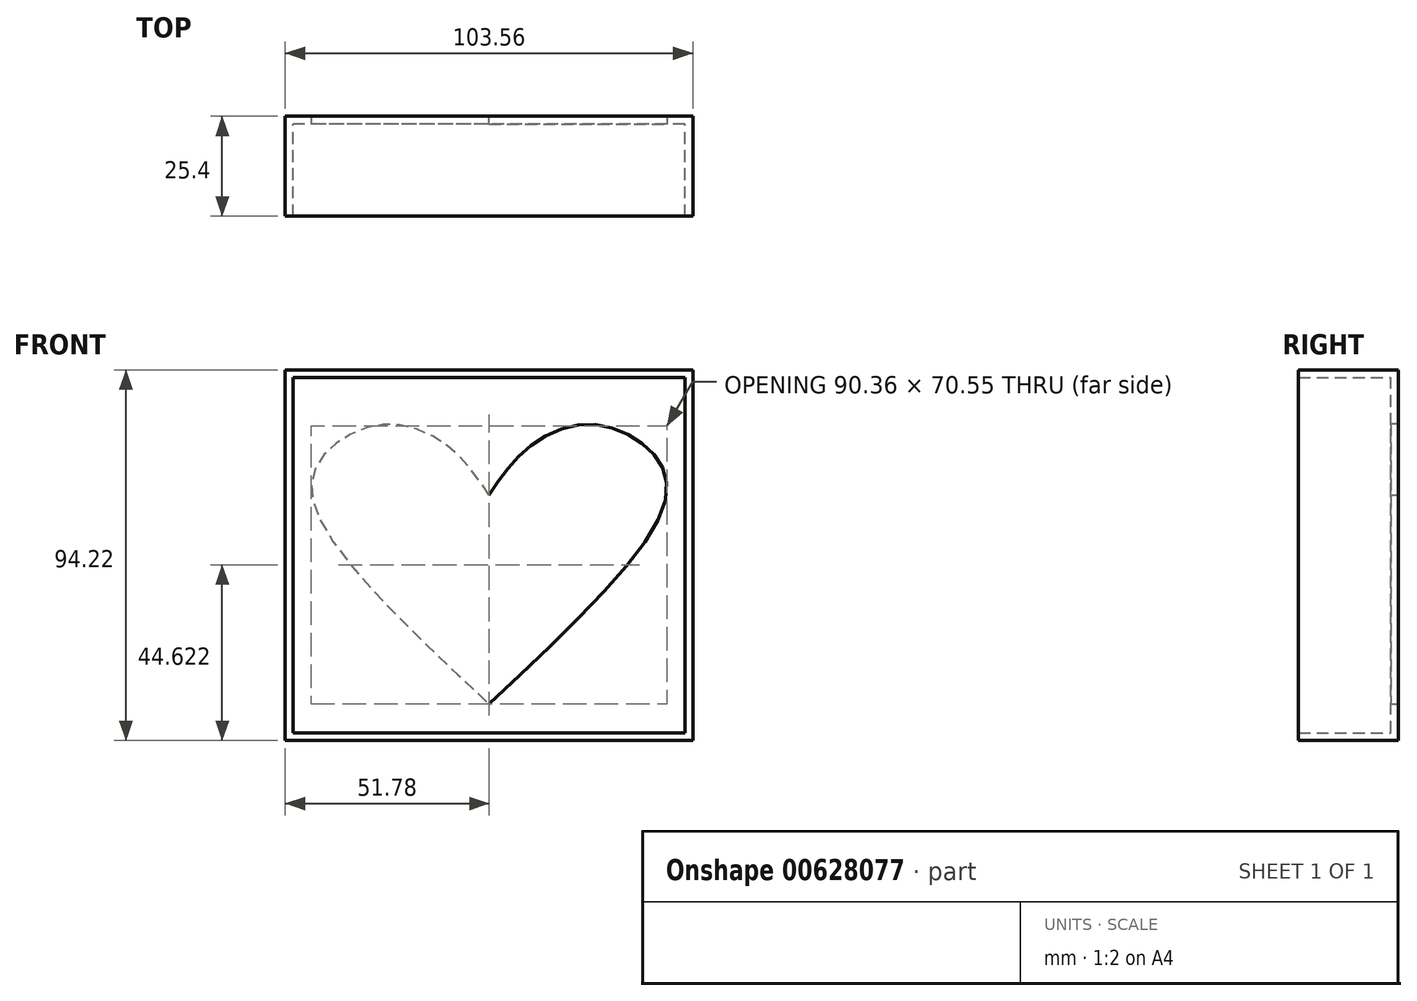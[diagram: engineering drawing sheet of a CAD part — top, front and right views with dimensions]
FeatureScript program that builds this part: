
annotation { "Feature Type Name" : "Feature", "Feature Type Description" : "" }
export const myFeature = defineFeature(function(context is Context, id is Id, definition is map)
    precondition{}
    {
        {
            var Q0;
            Q0=qCreatedBy(makeId("Front.planeOp"),FACE);
            var sketch = newSketch(context, id + "F0", { "sketchPlane" : qUnion([Q0])});
            skLineSegment(sketch, "E0.bottom", {"start": v(51.78, -47.1) * mm, "end": v(-51.78, -47.1) * mm});
            skLineSegment(sketch, "E0.top", {"start": v(51.78, 47.1) * mm, "end": v(-51.78, 47.1) * mm});
            skLineSegment(sketch, "E0.left", {"start": v(51.78, -47.1) * mm, "end": v(51.78, 47.1) * mm});
            skLineSegment(sketch, "E0.right", {"start": v(-51.78, -47.1) * mm, "end": v(-51.78, 47.1) * mm});
            skPoint(sketch, "E0.middle", {"position": v(0, 0) * mm});
            skSolve(sketch);
        }
        {
            var Q0;
            Q0=makeQuery(id+"F0.imprint","IMPRINT",FACE,{"disambiguationData":[TD([[makeQuery(id+"F0.imprint","IMPRINT",EDGE,{"derivedFrom":sQuery(id+"F0.wireOp",EDGE,"E0.bottom")}),-1.0]])]});
            extrude(context, id + "F1", {"entities" : qUnion([Q0]), "depth" : 25.4 * mm, "offsetDistance" : 25.4 * mm});
        }
        {
            var Q0;
            Q0=makeQuery(id+"F1.opExtrude","CAP_FACE",FACE,{"disambiguationData":[OSD([sQuery(id+"F0.wireOp",EDGE,"E0.bottom"),sQuery(id+"F0.wireOp",EDGE,"E0.top"),sQuery(id+"F0.wireOp",EDGE,"E0.left"),sQuery(id+"F0.wireOp",EDGE,"E0.right")])],"isStart":false});
            shell(context, id + "F2", {"entities" : qUnion([Q0]), "thickness" : 2 * mm});
        }
        {
            var Q0;
            Q0=makeQuery(id+"F1.opExtrude","CAP_FACE",FACE,{"disambiguationData":[OSD([sQuery(id+"F0.wireOp",EDGE,"E0.bottom"),sQuery(id+"F0.wireOp",EDGE,"E0.top"),sQuery(id+"F0.wireOp",EDGE,"E0.left"),sQuery(id+"F0.wireOp",EDGE,"E0.right")])],"isStart":true});
            var sketch = newSketch(context, id + "F3", { "sketchPlane" : qUnion([Q0])});
            skFitSpline(sketch, "E1", {"points": [v(0, 15.33) * mm, v(9.9, 27.3) * mm, v(25.61, 33.27) * mm, v(40.57, 26.92) * mm, v(44.68, 13.46) * mm, v(0, -37.76) * mm], "startDerivative": vector(52.69, 78.58) * mm, "endDerivative": vector(-181.02, -169.22) * mm});
            skFitSpline(sketch, "E2.MirrorCS", {"points": [v(0, 15.33) * mm, v(-9.9, 27.3) * mm, v(-25.61, 33.27) * mm, v(-40.57, 26.92) * mm, v(-44.68, 13.46) * mm, v(0, -37.76) * mm], "startDerivative": vector(-52.69, 78.58) * mm, "endDerivative": vector(181.02, -169.22) * mm});
            skSolve(sketch);
        }
        {
            var Q0;
            Q0=makeQuery(id+"F3.imprint","IMPRINT",FACE,{"disambiguationData":[TD([[makeQuery(id+"F3.imprint","IMPRINT",EDGE,{"derivedFrom":sQuery(id+"F3.wireOp",EDGE,"E1")}),-1.0]])]});
            extrude(context, id + "F4", {"entities" : qUnion([Q0]), "operationType" : NewBodyOperationType.REMOVE, "oppositeDirection" : true, "depth" : 25.4 * mm, "offsetDistance" : 25.4 * mm});
        }
    });
